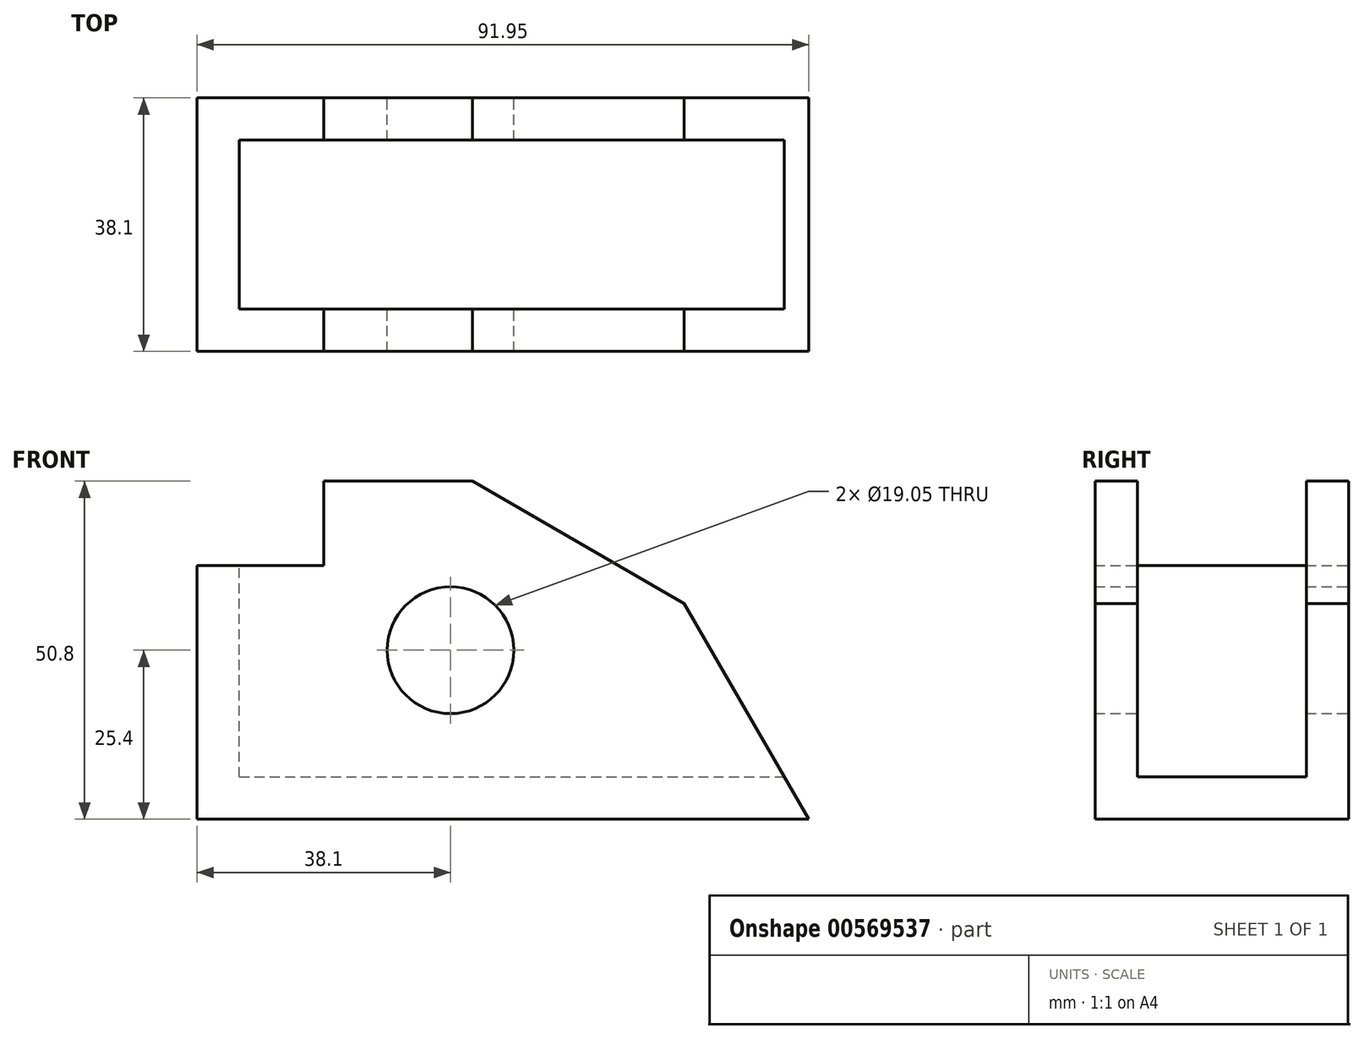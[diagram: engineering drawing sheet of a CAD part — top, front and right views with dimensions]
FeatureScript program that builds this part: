
annotation { "Feature Type Name" : "Feature", "Feature Type Description" : "" }
export const myFeature = defineFeature(function(context is Context, id is Id, definition is map)
    precondition{}
    {
        {
            var Q0;
            Q0=qCreatedBy(makeId("Front.planeOp"),FACE);
            var sketch = newSketch(context, id + "F0", { "sketchPlane" : qUnion([Q0])});
            skLineSegment(sketch, "E0.bottom", {"start": v(0, 0) * mm, "end": v(91.95, 0) * mm});
            skLineSegment(sketch, "E0.top", {"start": v(19.05, 50.8) * mm, "end": v(41.4, 50.8) * mm});
            skLineSegment(sketch, "E0.left", {"start": v(0, 0) * mm, "end": v(0, 50.8) * mm});
            skLineSegment(sketch, "E1.top", {"start": v(0, 38.1) * mm, "end": v(19.05, 38.1) * mm});
            skLineSegment(sketch, "E1.right", {"start": v(19.05, 50.8) * mm, "end": v(19.05, 38.1) * mm});
            skLineSegment(sketch, "E2", {"start": v(0, 0) * mm, "end": v(41.2, 0) * mm});
            skLineSegment(sketch, "E3.bottom", {"start": v(0, 0) * mm, "end": v(38.1, 0) * mm});
            skLineSegment(sketch, "E3.left", {"start": v(0, 0) * mm, "end": v(0, 25.4) * mm});
            skCircle(sketch, "E4", {"center": v(38.1, 25.4) * mm, "radius": 9.53 * mm});
            skLineSegment(sketch, "E5", {"start": v(41.4, 50.8) * mm, "end": v(73.23, 32.43) * mm});
            skLineSegment(sketch, "E6", {"start": v(91.95, 0) * mm, "end": v(73.23, 32.43) * mm});
            skSolve(sketch);
        }
        {
            var Q0;
            Q0=makeQuery(id+"F0.imprint","IMPRINT",FACE,{"disambiguationData":[TD([[makeQuery(id+"F0.imprint","IMPRINT",EDGE,{"derivedFrom":sQuery(id+"F0.wireOp",EDGE,"E0.bottom")}),1.0]])]});
            var Q1;
            Q1=makeQuery(id+"F0.imprint","IMPRINT",FACE,{"disambiguationData":[TD([[makeQuery(id+"F0.imprint","IMPRINT",EDGE,{"derivedFrom":sQuery(id+"F0.wireOp",EDGE,"E4")}),1.0]])]});
            extrude(context, id + "F1", {"entities" : qUnion([Q0, Q1]), "depth" : 38.1 * mm, "offsetDistance" : 25.4 * mm});
        }
        {
            var Q0;
            Q0=makeQuery(id+"F1.opExtrude","SWEPT_FACE",FACE,{"disambiguationData":[OSD([sQuery(id+"F0.wireOp",EDGE,"E6")])]});
            var Q1;
            Q1=makeQuery(id+"F1.opExtrude","SWEPT_FACE",FACE,{"disambiguationData":[OSD([sQuery(id+"F0.wireOp",EDGE,"E1.right")])]});
            var Q2;
            Q2=makeQuery(id+"F1.opExtrude","SWEPT_FACE",FACE,{"disambiguationData":[OSD([sQuery(id+"F0.wireOp",EDGE,"E1.top")])]});
            var Q3;
            Q3=makeQuery(id+"F1.opExtrude","SWEPT_FACE",FACE,{"disambiguationData":[OSD([sQuery(id+"F0.wireOp",EDGE,"E0.top")])]});
            var Q4;
            Q4=makeQuery(id+"F1.opExtrude","SWEPT_FACE",FACE,{"disambiguationData":[OSD([sQuery(id+"F0.wireOp",EDGE,"E5")])]});
            shell(context, id + "F2", {"entities" : qUnion([Q0, Q1, Q2, Q3, Q4]), "thickness" : 6.35 * mm});
        }
        {
            var Q0;
            Q0=makeQuery(id+"F0.imprint","IMPRINT",FACE,{"disambiguationData":[TD([[makeQuery(id+"F0.imprint","IMPRINT",EDGE,{"derivedFrom":sQuery(id+"F0.wireOp",EDGE,"E4")}),1.0]])]});
            var Q1;
            Q1=sQuery(id+"F0.wireOp",EDGE,"E4");
            extrude(context, id + "F3", {"entities" : qUnion([Q0]), "operationType" : NewBodyOperationType.REMOVE, "surfaceEntities" : qUnion([Q1]), "endBound" : BoundingType.THROUGH_ALL, "depth" : 25.4 * mm, "offsetDistance" : 25.4 * mm});
        }
    });
